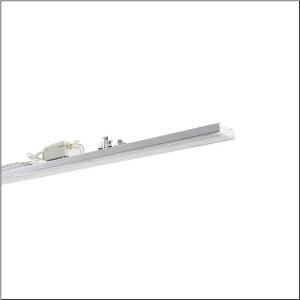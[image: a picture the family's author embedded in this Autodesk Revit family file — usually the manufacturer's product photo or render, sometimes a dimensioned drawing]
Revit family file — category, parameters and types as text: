
# Revit family: licross_r__21_recessed_mo_52tl127n485g_113a
name_source: partatom
category: Lighting Fixtures
units: mm (PartAtom-declared; Revit-internal decimal feet)

## family parameters
Cut with Voids When Loaded = No
Host = Face
Light Source = No
Part Type = Normal
Room Calculation Point = No
Round Connector Dimension = Use Diameter
Shared = No

## types (1)
- Licross® 21 Recessed MO (1 x LED, 8820 lm, 47.9 W, 4000K)
    Apparent Load = 48 VA
    CIE Flux Codes = 72 92 99 100 100
    Color Rendering = 80
    Color Temperature = 4000K
    Default Elevation = 1800 mm
    Description = Licross® 21 Recessed MO, luminaire insert, of sheet steel, galvanised, coil coated, white, length: 1.500mm, width: 66mm, height: 67mm, LED rated luminous flux: 8.820lm, light colour: 840, control gear: ON/OFF, with plug, 3-pole, with phase selection, mains connection: 220..240V, AC, 50/60Hz, rated input power: 48W, halogen-free wiring, primary optical cover: cover, of PMMA, light emission: direct distribution, primary light characteristic: symmetric, protection rating (complete): IP40, insulation class (complete): insulation class I (protective earthing), certification: CE, ENEC, VDE, UKCA, protection symbol: D if used in an environment without relevant dust loads with corresponding accessories, impact resistance: IK06, permissible ambient temperature for indoor applications: -35..+40°C, corresponds to IFS (International Featured Standards) requirements for safety and quality in the food industry, reducing of maximum allowable ambient temperature of 5°C with ceiling mounting, LABS conformity tested according to VDMA 24364:2018-05, packaging unit: 1 piece
    Height = 58 mm
    Lamp = 1 x LED
    Lamp Light Flux = 8820 lm
    Lamp Power = 47.9 W
    Lamp count = 1
    Length = 1500 mm
    Luminous efficacy = 184 lm/W
    Manufacturer = Siteco
    ModVariant = No
    Model = 52TL127N485G
    Mounting Place = Ceiling
    Mounting Type = Pendant
    Number of Poles = 1
    OnlyDefault = Yes
    Power Factor = 1
    Product Name = Licross® 21 Recessed MO
    Product group = luminaire insert
    ProductGroupID = 901
    Protection Class = Protection class I
    Protection Degree = IP 40
    RLX_Detail_Level = 1
    RLX_Emergency_Light_Flux = 0 lm
    RLX_Emergency_Type = 0
    RLX_Emergency_Type_DB = No
    RlxData = <blob elided: 20925 chars, md5=9a91f6e6>
    Socket = socket
    Standby Power = 0 W
    System Light Flux = 8820 lm
    System Power = 48 W
    Type Comments = Product without accessories
    Type Image = l_1296930.jpg
    URL = http://relux.com
    VarID = ---
    Voltage = 0 V
    Weight = 0.00 kg
    Width = 66 mm

## geometry (parser evidence)
native form markers: Blend x4, Sweep x12
no freeform markers — native parametric forms only
